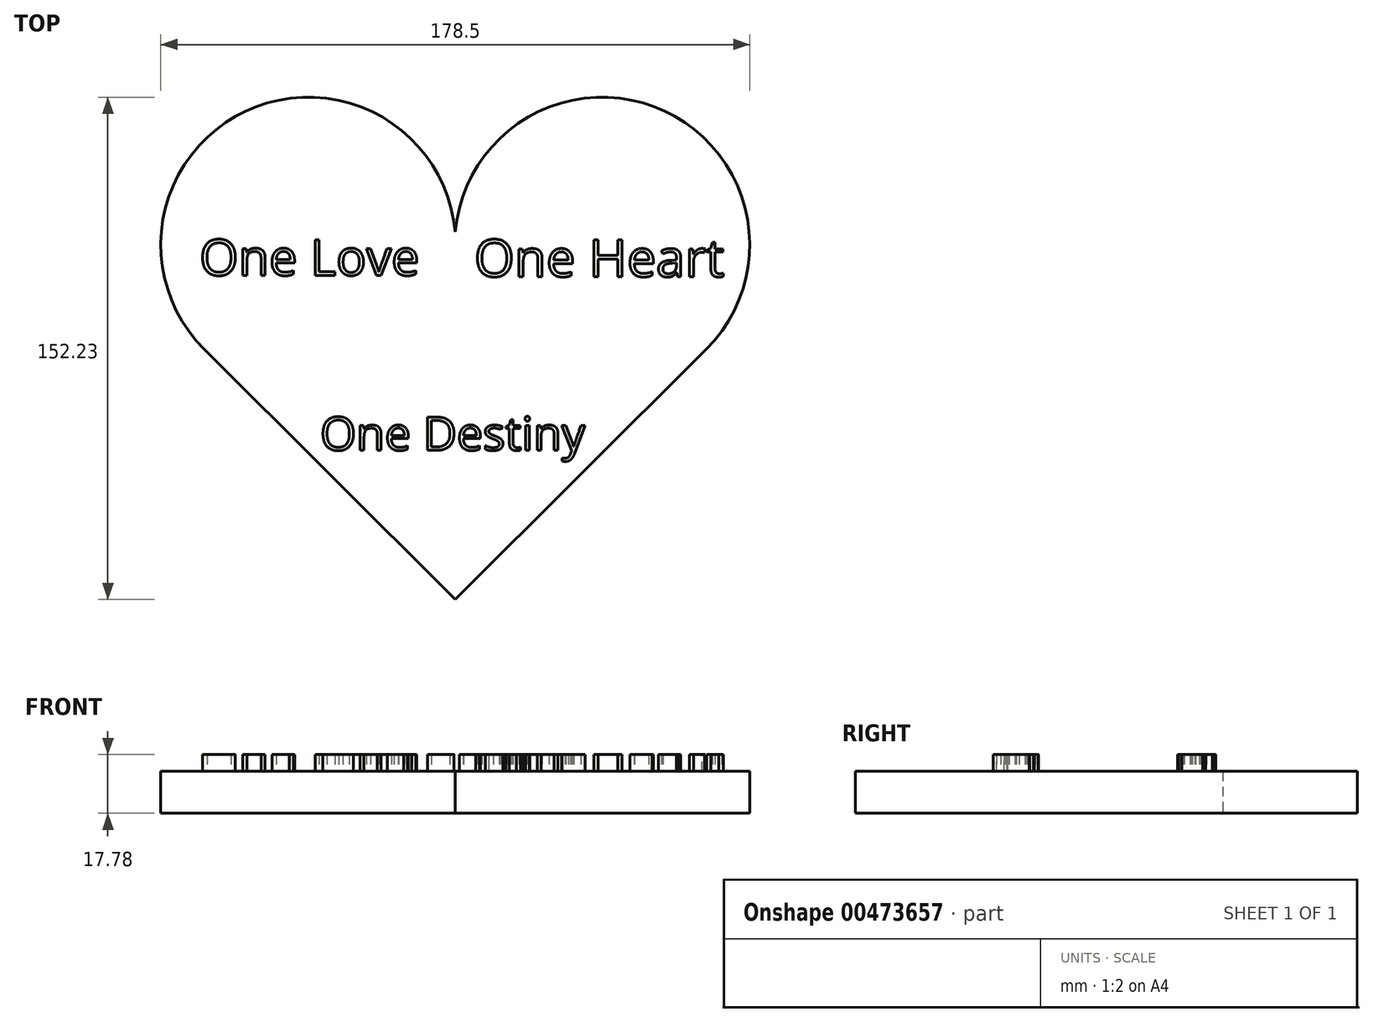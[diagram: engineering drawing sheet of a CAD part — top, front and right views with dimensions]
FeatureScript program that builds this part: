
annotation { "Feature Type Name" : "Feature", "Feature Type Description" : "" }
export const myFeature = defineFeature(function(context is Context, id is Id, definition is map)
    precondition{}
    {
        {
            var Q0;
            Q0=qCreatedBy(makeId("Top.planeOp"),FACE);
            var sketch = newSketch(context, id + "F0", { "sketchPlane" : qUnion([Q0])});
            skLineSegment(sketch, "E0", {"start": v(0, -75.85) * mm, "end": v(76.1, 0) * mm});
            skLineSegment(sketch, "E1", {"start": v(-76.1, 0) * mm, "end": v(0, -75.85) * mm});
            skArc(sketch, "E2", {"start": v(76.1, 0) * mm, "mid": v(59.89, 73.66) * mm, "end": v(0, 27.8) * mm});
            skArc(sketch, "E3", {"start": v(-76.1, 0) * mm, "mid": v(-59.88, 73.66) * mm, "end": v(0, 27.8) * mm});
            skSolve(sketch);
        }
        {
            var Q0;
            {var subQ4=sQuery(id+"F0.wireOp",EDGE,"E0");Q0=makeQuery(id+"F0.imprint","IMPRINT",FACE,{"disambiguationData":[TD([[makeQuery(id+"F0.imprint","IMPRINT",EDGE,{"derivedFrom":subQ4}),1.0]])]});}
            var sketch = newSketch(context, id + "F1", { "sketchPlane" : qUnion([Q0])});
            skText(sketch, "E4", { "text": "One Destiny", "fontName": "OpenSans-Regular.ttf"});
            const initialGuessF1  = {"E4": [-0.04096, -0.03063, 1, 0, 0.01014]};
            skSetInitialGuess(sketch, initialGuessF1);
            skSolve(sketch);
        }
        {
            var Q0;
            Q0=makeQuery(id+"F1.imprint","IMPRINT",FACE,{"disambiguationData":[TD([[makeQuery(id+"F1.imprint","IMPRINT",EDGE,{"derivedFrom":sQuery(id+"F1.wireOp",EDGE,"E4.sketch_text.stroke-0")}),1.0]])]});
            var sketch = newSketch(context, id + "F2", { "sketchPlane" : qUnion([Q0])});
            skText(sketch, "E5", { "text": "One Love", "fontName": "OpenSans-Regular.ttf"});
            const initialGuessF2  = {"E5": [-0.07752, 0.02239, 1, 0, 0.01091]};
            skSetInitialGuess(sketch, initialGuessF2);
            skSolve(sketch);
        }
        {
            var Q0;
            Q0=makeQuery(id+"F1.imprint","IMPRINT",FACE,{"disambiguationData":[TD([[makeQuery(id+"F1.imprint","IMPRINT",EDGE,{"derivedFrom":sQuery(id+"F1.wireOp",EDGE,"E4.sketch_text.stroke-0")}),1.0]])]});
            var sketch = newSketch(context, id + "F3", { "sketchPlane" : qUnion([Q0])});
            skText(sketch, "E6", { "text": "One Heart", "fontName": "OpenSans-Regular.ttf"});
            const initialGuessF3  = {"E6": [0.00574, 0.022, 1, 0, 0.0113]};
            skSetInitialGuess(sketch, initialGuessF3);
            skSolve(sketch);
        }
        {
            var Q0;
            Q0 = qSketchRegion(id + "F0", true);
            extrude(context, id + "F4", {"entities" : qUnion([Q0]), "depth" : 12.7 * mm});
        }
        {
            var Q0;
            Q0 = qSketchRegion(id + "F1", true);
            var Q1;
            Q1 = qSketchRegion(id + "F2", true);
            var Q2;
            Q2 = qSketchRegion(id + "F3", true);
            extrude(context, id + "F5", {"entities" : qUnion([Q0, Q1, Q2]), "operationType" : NewBodyOperationType.ADD, "depth" : 17.78 * mm});
        }
    });
